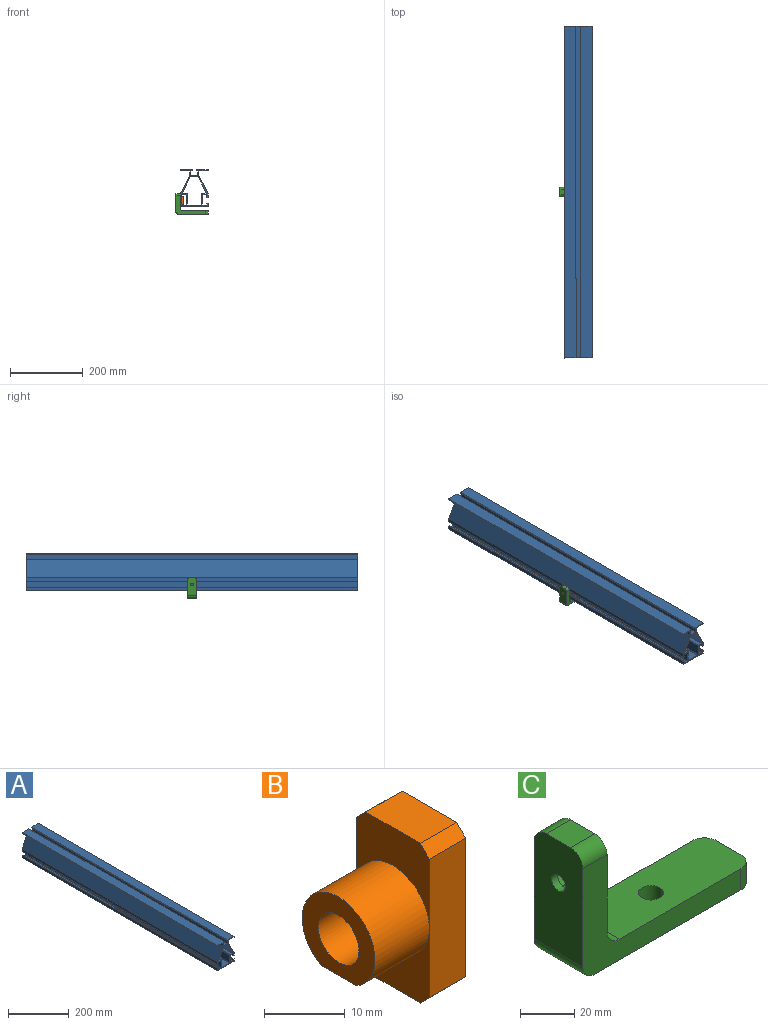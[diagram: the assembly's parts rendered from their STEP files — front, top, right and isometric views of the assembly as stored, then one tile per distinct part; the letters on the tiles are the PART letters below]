
ASSEMBLY  parts=3 mates=2
PART A: 62 faces, bbox 76.2x914.4x101.6 mm
  f0: plane 914.4x31.75mm, normal (0,0,1), area 29032.2mm2, adj f1,f2,f8,f39
  f1: plane 101.6x76.2mm, normal (0,1,0), area 1343.7mm2, adj f0,f3,f4,f5,f6,f7,f8,f9
  f2: plane 101.6x76.2mm, normal (0,-1,0), area 1343.7mm2, adj f0,f3,f4,f5,f6,f7,f8,f9
  f3: plane 914.4x9.53mm, normal (1,0,0), area 8709.7mm2, adj f1,f2,f7,f28
  f4: plane 914.4x10.41mm, normal (1,0,0), area 9522.6mm2, adj f1,f2,f26,f29
  f5: plane 914.4x9.53mm, normal (-1,0,0), area 8709.7mm2, adj f1,f2,f7,f14
  f6: plane 914.4x10.41mm, normal (-1,0,0), area 9522.6mm2, adj f1,f2,f11,f15
  f7: plane 914.4x76.2mm, normal (0,0,-1), area 69677.3mm2, adj f1,f2,f3,f5
  f8: plane 914.4x3.18mm, normal (1,0,0), area 2903.2mm2, adj f0,f1,f2,f25
  f9: plane 914.4x31.75mm, normal (0,0,1), area 29032.2mm2, adj f1,f2,f10,f40
  f10: plane 914.4x3.18mm, normal (-1,0,0), area 2903.2mm2, adj f1,f2,f9,f12
  f11: plane 914.4x50.8mm, normal (-0.89,0,0.45), area 51934.4mm2, adj f1,f2,f6,f13
  f12: plane 914.4x25.4mm, normal (0,0,-1), area 23225.8mm2, adj f1,f2,f10,f13
  f13: plane 914.4x12.7mm, normal (-1,0,0), area 11612.9mm2, adj f1,f2,f11,f12
  f14: plane 914.4x3.18mm, normal (0,0,1), area 2903.2mm2, adj f1,f2,f5,f16
  f15: plane 914.4x3.18mm, normal (0,0,-1), area 2903.2mm2, adj f1,f2,f6,f24
  f16: plane 914.4x5.08mm, normal (1,0,0), area 4645.2mm2, adj f1,f2,f14,f17
  f17: cylinder r=1.27mm len=914.4mm, axis (0,-1,0), area 1824.1mm2, adj f1,f2,f16,f18
  f18: plane 914.4x10.16mm, normal (0,0,1), area 9290.3mm2, adj f1,f2,f17,f19
  f19: cylinder r=1.27mm len=914.4mm, axis (0,-1,0), area 1824.1mm2, adj f1,f2,f18,f20
  f20: plane 914.4x26.42mm, normal (-1,0,0), area 24154.8mm2, adj f1,f2,f19,f21
  f21: cylinder r=1.27mm len=914.4mm, axis (0,-1,0), area 1824.1mm2, adj f1,f2,f20,f22
  f22: plane 914.4x10.16mm, normal (0,0,-1), area 9290.3mm2, adj f1,f2,f21,f23
  f23: cylinder r=1.27mm len=914.4mm, axis (0,-1,0), area 1824.1mm2, adj f1,f2,f22,f24
  f24: plane 914.4x6.35mm, normal (1,0,0), area 5806.4mm2, adj f1,f2,f15,f23
  f25: plane 914.4x25.4mm, normal (0,0,-1), area 23225.8mm2, adj f1,f2,f8,f27
  f26: plane 914.4x50.8mm, normal (0.89,0,0.45), area 51934.4mm2, adj f1,f2,f4,f27
  f27: plane 914.4x12.7mm, normal (1,0,0), area 11612.9mm2, adj f1,f2,f25,f26
  f28: plane 914.4x3.18mm, normal (0,0,1), area 2903.2mm2, adj f1,f2,f3,f38
  f29: plane 914.4x3.18mm, normal (0,0,-1), area 2903.2mm2, adj f1,f2,f4,f30
  f30: plane 914.4x6.35mm, normal (-1,0,0), area 5806.4mm2, adj f1,f2,f29,f31
  f31: cylinder r=1.27mm len=914.4mm, axis (0,-1,0), area 1824.1mm2, adj f1,f2,f30,f32
  f32: plane 914.4x10.16mm, normal (0,0,-1), area 9290.3mm2, adj f1,f2,f31,f33
  f33: cylinder r=1.27mm len=914.4mm, axis (0,-1,0), area 1824.1mm2, adj f1,f2,f32,f34
  f34: plane 914.4x26.42mm, normal (1,0,0), area 24154.8mm2, adj f1,f2,f33,f35
  f35: cylinder r=1.27mm len=914.4mm, axis (0,-1,0), area 1824.1mm2, adj f1,f2,f34,f36
  f36: plane 914.4x10.16mm, normal (0,0,1), area 9290.3mm2, adj f1,f2,f35,f37
  f37: cylinder r=1.27mm len=914.4mm, axis (0,-1,0), area 1824.1mm2, adj f1,f2,f36,f38
  f38: plane 914.4x5.08mm, normal (-1,0,0), area 4645.2mm2, adj f1,f2,f28,f37
  f39: plane 914.4x3.18mm, normal (-1,0,0), area 2903.2mm2, adj f0,f1,f2,f45
  f40: plane 914.4x3.18mm, normal (1,0,0), area 2903.2mm2, adj f1,f2,f9,f41
  f41: plane 914.4x3.18mm, normal (0,0,-1), area 2903.2mm2, adj f1,f2,f40,f42
  f42: plane 914.4x12.7mm, normal (1,0,0), area 11612.9mm2, adj f1,f2,f41,f43
  f43: plane 914.4x19.05mm, normal (0,0,1), area 17419.3mm2, adj f1,f2,f42,f44
  f44: plane 914.4x12.7mm, normal (-1,0,0), area 11612.9mm2, adj f1,f2,f43,f45
  f45: plane 914.4x3.18mm, normal (0,0,-1), area 2903.2mm2, adj f1,f2,f39,f44
  f46: plane 914.4x29.59mm, normal (1,0,0), area 27058mm2, adj f1,f2,f47,f61
  f47: cylinder r=1.27mm len=914.4mm, axis (0,-1,0), area 1824.1mm2, adj f1,f2,f46,f48
  f48: plane 914.4x35.56mm, normal (0,0,1), area 32516.1mm2, adj f1,f2,f47,f49
  f49: cylinder r=1.27mm len=914.4mm, axis (0,-1,0), area 1824.1mm2, adj f1,f2,f48,f50
  f50: plane 914.4x29.59mm, normal (-1,0,0), area 27058mm2, adj f1,f2,f49,f51
  f51: cylinder r=1.27mm len=914.4mm, axis (0,-1,0), area 1824.1mm2, adj f1,f2,f50,f52
  f52: plane 914.4x11.99mm, normal (0,0,1), area 10958.9mm2, adj f1,f2,f51,f53
  f53: cylinder r=1.27mm len=914.4mm, axis (0,-1,0), area 2362.6mm2, adj f1,f2,f52,f54
  f54: plane 914.4x44.7mm, normal (-0.89,0,-0.45), area 45702.3mm2, adj f1,f2,f53,f55
  f55: cylinder r=1.27mm len=914.4mm, axis (0,-1,0), area 1285.7mm2, adj f1,f2,f54,f56
  f56: plane 914.4x19.91mm, normal (0,0,-1), area 18201.8mm2, adj f1,f2,f55,f57
  f57: cylinder r=1.27mm len=914.4mm, axis (0,-1,0), area 1285.7mm2, adj f1,f2,f56,f58
  f58: plane 914.4x44.7mm, normal (0.89,0,-0.45), area 45702.3mm2, adj f1,f2,f57,f59
  f59: cylinder r=1.27mm len=914.4mm, axis (0,-1,0), area 2362.6mm2, adj f1,f2,f58,f60
  f60: plane 914.4x11.99mm, normal (0,0,1), area 10958.9mm2, adj f1,f2,f59,f61
  f61: cylinder r=1.27mm len=914.4mm, axis (0,-1,0), area 1824.1mm2, adj f1,f2,f46,f60
PART B: 17 faces, bbox 15.9x12.7x24.2 mm
  f0: cylinder r=3.57mm len=7.93mm, axis (1,0,0), area 177.7mm2, adj f2,f16
  f1: cylinder r=6.35mm len=12.7mm, axis (1,0,0), area 317.2mm2, adj f2,f3,f5,f14
  f2: plane 12.7x11.86mm, normal (-1,0,0), area 83.1mm2, adj f0,f1,f14
  f3: plane 12.7x12.09mm, normal (-1,0,0), area 91.2mm2, adj f1,f6,f8,f9,f10,f11,f14
  f4: plane 9.5x6.35mm, normal (0,0,1), area 60.3mm2, adj f5,f7,f12,f13
  f5: plane 12.7x12.09mm, normal (-1,0,0), area 87.6mm2, adj f1,f4,f8,f9,f12,f13
  f6: plane 9.5x6.35mm, normal (0,0,-1), area 60.3mm2, adj f3,f7,f10,f11
  f7: plane 24.18x12.7mm, normal (1,0,0), area 234.8mm2, adj f4,f6,f8,f9,f10,f11,f12,f13
  f8: plane 20.98x6.35mm, normal (0,1,0), area 133.2mm2, adj f3,f5,f7,f10,f12
  f9: plane 20.98x6.35mm, normal (0,-1,0), area 133.2mm2, adj f3,f5,f7,f11,f13
  f10: plane 6.35x1.6mm, normal (0,0.71,-0.71), area 14.4mm2, adj f3,f6,f7,f8
  f11: plane 6.35x1.6mm, normal (0,-0.71,-0.71), area 14.4mm2, adj f3,f6,f7,f9
  f12: plane 6.35x1.6mm, normal (0,0.71,0.71), area 14.4mm2, adj f4,f5,f7,f8
  f13: plane 6.35x1.6mm, normal (0,-0.71,0.71), area 14.4mm2, adj f4,f5,f7,f9
  f14: plane 9.53x6.31mm, normal (0,0,-1), area 60.1mm2, adj f1,f2,f3
  f15: cylinder r=4.62mm len=9.25mm, axis (1,0,0), area 230.9mm2, adj f7,f16
  f16: plane 9.25x9.25mm, normal (1,0,0), area 27.1mm2, adj f0,f15
PART C: 19 faces, bbox 88.9x25.4x57.2 mm
  f0: plane 41.28x25.4mm, normal (1,0,0), area 898.8mm2, adj f1,f2,f3,f10,f12,f13,f17,f18
  f1: plane 12.7x12.7mm, normal (0,0,1), area 161.3mm2, adj f0,f4,f12,f13
  f2: plane 82.55x50.8mm, normal (0,1,0), area 1310.5mm2, adj f0,f4,f7,f8,f10,f11,f12,f16
  f3: plane 82.55x50.8mm, normal (0,-1,0), area 1310.5mm2, adj f0,f4,f7,f8,f10,f11,f13,f15
  f4: plane 50.8x25.4mm, normal (-1,0,0), area 1233mm2, adj f1,f2,f3,f6,f11,f12,f13
  f5: plane 13.16x12.32mm, normal (1,0,0), area 92.3mm2, adj f6,f17,f18
  f6: cylinder r=3.57mm len=7.14mm, axis (-1,0,0), area 71.2mm2, adj f4,f5
  f7: plane 82.55x25.4mm, normal (0,0,-1), area 2012.3mm2, adj f2,f3,f9,f11,f14,f15,f16
  f8: plane 69.85x25.4mm, normal (0,0,1), area 1689.7mm2, adj f2,f3,f9,f10,f14,f15,f16
  f9: plane 12.7x9.53mm, normal (1,0,0), area 121mm2, adj f7,f8,f15,f16
  f10: cylinder r=6.35mm len=25.4mm, axis (0,1,0), area 253.4mm2, adj f0,f2,f3,f8
  f11: cylinder r=6.35mm len=25.4mm, axis (0,-1,0), area 253.4mm2, adj f2,f3,f4,f7
  f12: cylinder r=6.35mm len=12.7mm, axis (-1,0,0), area 126.7mm2, adj f0,f1,f2,f4
  f13: cylinder r=6.35mm len=12.7mm, axis (1,0,0), area 126.7mm2, adj f0,f1,f3,f4
  f14: cylinder r=4.62mm len=9.53mm, axis (0,0,-1), area 276.7mm2, adj f7,f8
  f15: cylinder r=6.35mm len=9.53mm, axis (0,0,-1), area 95mm2, adj f3,f7,f8,f9
  f16: cylinder r=6.35mm len=9.53mm, axis (0,0,1), area 95mm2, adj f2,f7,f8,f9
  f17: plane 9.53x6.43mm, normal (0,0,1), area 61.2mm2, adj f0,f5,f18
  f18: cylinder r=6.58mm len=13.16mm, axis (1,0,0), area 329.8mm2, adj f0,f5,f17
PLACE A t=(244.57,-596.43,286.73)mm
PLACE B t=(239.49,-145.58,286.14)mm fixed
PLACE C t=(245.84,-145.58,286.14)mm
MATE planar C.f0 <-> A.f6  axis (1,0,0) through (206.47,-139.23,250.78)mm
MATE planar B.f3 <-> A.f16  axis (-1,0,0) through (209.65,-139.23,244.79)mm
